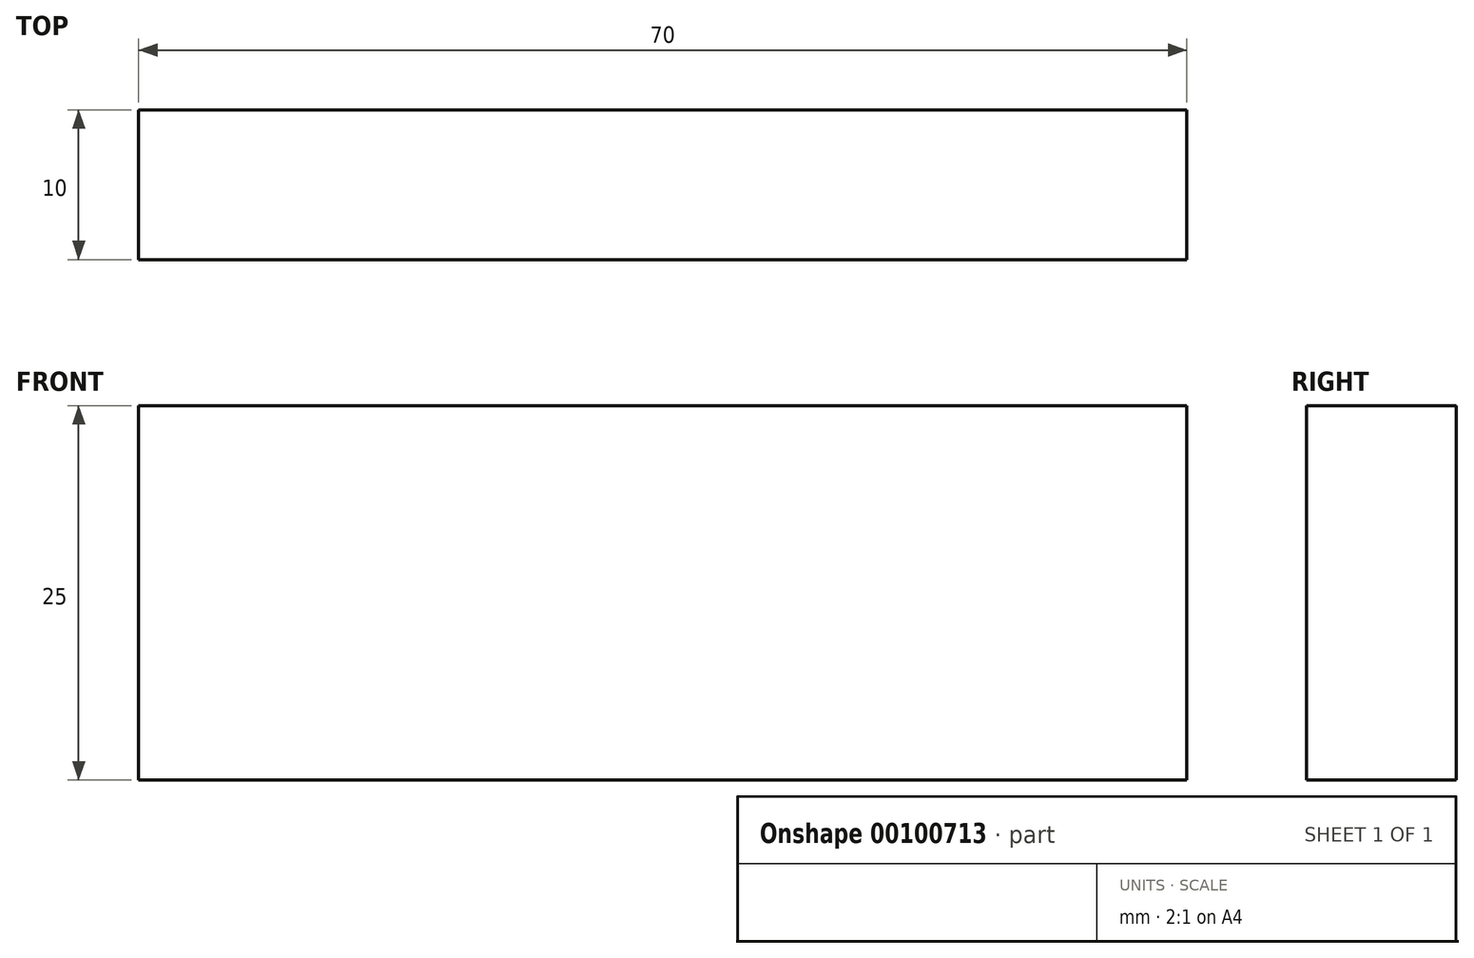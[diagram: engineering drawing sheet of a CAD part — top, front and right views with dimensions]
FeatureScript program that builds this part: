
annotation { "Feature Type Name" : "Feature", "Feature Type Description" : "" }
export const myFeature = defineFeature(function(context is Context, id is Id, definition is map)
    precondition{}
    {
        {
            var Q0;
            Q0=qCreatedBy(makeId("Front.planeOp"),FACE);
            var sketch = newSketch(context, id + "F0", { "sketchPlane" : qUnion([Q0])});
            skLineSegment(sketch, "E0.bottom", {"start": v(0, 0) * mm, "end": v(-70, 0) * mm});
            skLineSegment(sketch, "E0.top", {"start": v(0, 25) * mm, "end": v(-70, 25) * mm});
            skLineSegment(sketch, "E0.left", {"start": v(0, 0) * mm, "end": v(0, 25) * mm});
            skLineSegment(sketch, "E0.right", {"start": v(-70, 0) * mm, "end": v(-70, 25) * mm});
            skSolve(sketch);
        }
        {
            var Q0;
            Q0=makeQuery(id+"F0.imprint","IMPRINT",FACE,{"disambiguationData":[TD([[makeQuery(id+"F0.imprint","IMPRINT",EDGE,{"derivedFrom":sQuery(id+"F0.wireOp",EDGE,"E0.bottom")}),-1.0]])]});
            extrude(context, id + "F1", {"entities" : qUnion([Q0]), "depth" : 10 * mm});
        }
    });
